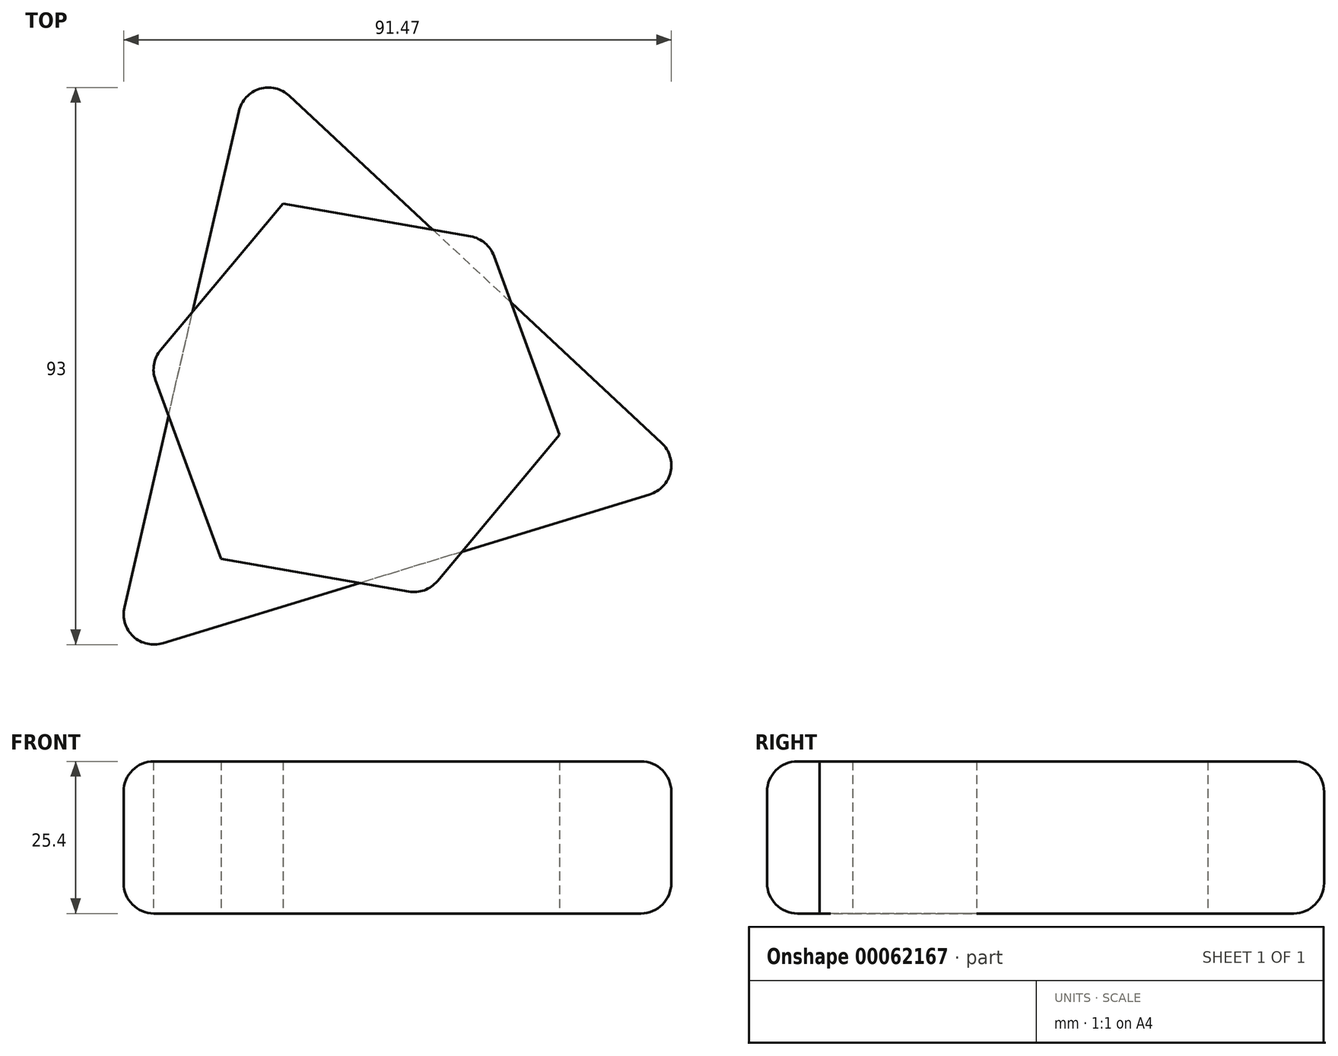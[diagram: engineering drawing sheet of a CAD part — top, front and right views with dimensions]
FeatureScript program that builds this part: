
annotation { "Feature Type Name" : "Feature", "Feature Type Description" : "" }
export const myFeature = defineFeature(function(context is Context, id is Id, definition is map)
    precondition{}
    {
        {
            var Q0;
            Q0=qCreatedBy(makeId("Top.planeOp"),FACE);
            var sketch = newSketch(context, id + "F0", { "sketchPlane" : qUnion([Q0])});
            skCircle(sketch, "E0.cCircle", {"center": v(0, 0) * mm, "radius": 29.62 * mm, "construction": true});
            skLineSegment(sketch, "E0.0", {"start": v(57.73, -13.33) * mm, "end": v(-40.4, -43.33) * mm});
            skLineSegment(sketch, "E0.1", {"start": v(-40.4, -43.33) * mm, "end": v(-17.32, 56.66) * mm});
            skLineSegment(sketch, "E0.2", {"start": v(-17.32, 56.66) * mm, "end": v(57.73, -13.33) * mm});
            skPoint(sketch, "E0.0.midPoint", {"position": v(8.66, -28.33) * mm});
            skSolve(sketch);
        }
        {
            var Q0;
            Q0=qCreatedBy(makeId("Top.planeOp"),FACE);
            var sketch = newSketch(context, id + "F1", { "sketchPlane" : qUnion([Q0])});
            skCircle(sketch, "E1.cCircle", {"center": v(0, 0) * mm, "radius": 30.1 * mm, "construction": true});
            skLineSegment(sketch, "E1.0", {"start": v(34.24, -5.97) * mm, "end": v(11.95, -32.64) * mm});
            skLineSegment(sketch, "E1.1", {"start": v(11.95, -32.64) * mm, "end": v(-22.3, -26.67) * mm});
            skLineSegment(sketch, "E1.2", {"start": v(-22.3, -26.67) * mm, "end": v(-34.24, 5.97) * mm});
            skLineSegment(sketch, "E1.3", {"start": v(-34.24, 5.97) * mm, "end": v(-11.95, 32.64) * mm});
            skLineSegment(sketch, "E1.4", {"start": v(-11.95, 32.64) * mm, "end": v(22.3, 26.67) * mm});
            skLineSegment(sketch, "E1.5", {"start": v(22.3, 26.67) * mm, "end": v(34.24, -5.97) * mm});
            skPoint(sketch, "E1.0.midPoint", {"position": v(23.1, -19.3) * mm});
            skSolve(sketch);
        }
        {
            var Q0;
            Q0=makeQuery(id+"F0.imprint","IMPRINT",FACE,{"disambiguationData":[TD([[makeQuery(id+"F0.imprint","IMPRINT",EDGE,{"derivedFrom":sQuery(id+"F0.wireOp",EDGE,"E0.0")}),-1.0]])]});
            var Q1;
            Q1=makeQuery(id+"F1.imprint","IMPRINT",FACE,{"disambiguationData":[TD([[makeQuery(id+"F1.imprint","IMPRINT",EDGE,{"derivedFrom":sQuery(id+"F1.wireOp",EDGE,"E1.0")}),-1.0]])]});
            extrude(context, id + "F2", {"entities" : qUnion([Q0, Q1]), "depth" : 25.4 * mm});
        }
        {
            var Q0;
            Q0=makeQuery(id+"F2.opExtrude","CAP_EDGE",EDGE,{"disambiguationData":[OSD([sQuery(id+"F0.wireOp",EDGE,"E0.2")])],"isStart":false});
            var Q1;
            Q1=makeQuery(id+"F2.opExtrude","CAP_EDGE",EDGE,{"disambiguationData":[OSD([sQuery(id+"F0.wireOp",EDGE,"E0.0")])],"isStart":false});
            var Q2;
            Q2=makeQuery(id+"F2.opExtrude","CAP_EDGE",EDGE,{"disambiguationData":[OSD([sQuery(id+"F0.wireOp",EDGE,"E0.1")])],"isStart":false});
            var Q3;
            Q3=makeQuery(id+"F2.opExtrude","SWEPT_EDGE",EDGE,{"disambiguationData":[OSD([sQuery(id+"F1.wireOp",EDGE,"E1.0"),sQuery(id+"F1.wireOp",EDGE,"E1.1")])]});
            var Q4;
            Q4=makeQuery(id+"F2.opExtrude","SWEPT_EDGE",EDGE,{"disambiguationData":[OSD([sQuery(id+"F1.wireOp",EDGE,"E1.4"),sQuery(id+"F1.wireOp",EDGE,"E1.5")])]});
            var Q5;
            Q5=makeQuery(id+"F2.opExtrude","SWEPT_EDGE",EDGE,{"disambiguationData":[OSD([sQuery(id+"F1.wireOp",EDGE,"E1.2"),sQuery(id+"F1.wireOp",EDGE,"E1.3")])]});
            var Q6;
            Q6=makeQuery(id+"F2.opExtrude","SWEPT_EDGE",EDGE,{"disambiguationData":[OSD([sQuery(id+"F0.wireOp",EDGE,"E0.0"),sQuery(id+"F0.wireOp",EDGE,"E0.1")])]});
            var Q7;
            Q7=makeQuery(id+"F2.opExtrude","SWEPT_EDGE",EDGE,{"disambiguationData":[OSD([sQuery(id+"F0.wireOp",EDGE,"E0.0"),sQuery(id+"F0.wireOp",EDGE,"E0.2")])]});
            var Q8;
            Q8=makeQuery(id+"F2.opExtrude","SWEPT_FACE",FACE,{"disambiguationData":[OSD([sQuery(id+"F0.wireOp",EDGE,"E0.1")])]});
            fillet(context, id + "F3", {"entities" : qUnion([Q0, Q1, Q2, Q3, Q4, Q5, Q6, Q7, Q8]), "radius" : 5.08 * mm, "tangentPropagation" : true, "allowEdgeOverflow" : false});
        }
        {
            var Q0;
            Q0=makeQuery(id+"F2.opExtrude","CAP_EDGE",EDGE,{"disambiguationData":[OSD([sQuery(id+"F0.wireOp",EDGE,"E0.2")])],"isStart":true});
            fillet(context, id + "F4", {"entities" : qUnion([Q0]), "radius" : 5.08 * mm, "tangentPropagation" : true, "allowEdgeOverflow" : false});
        }
    });
